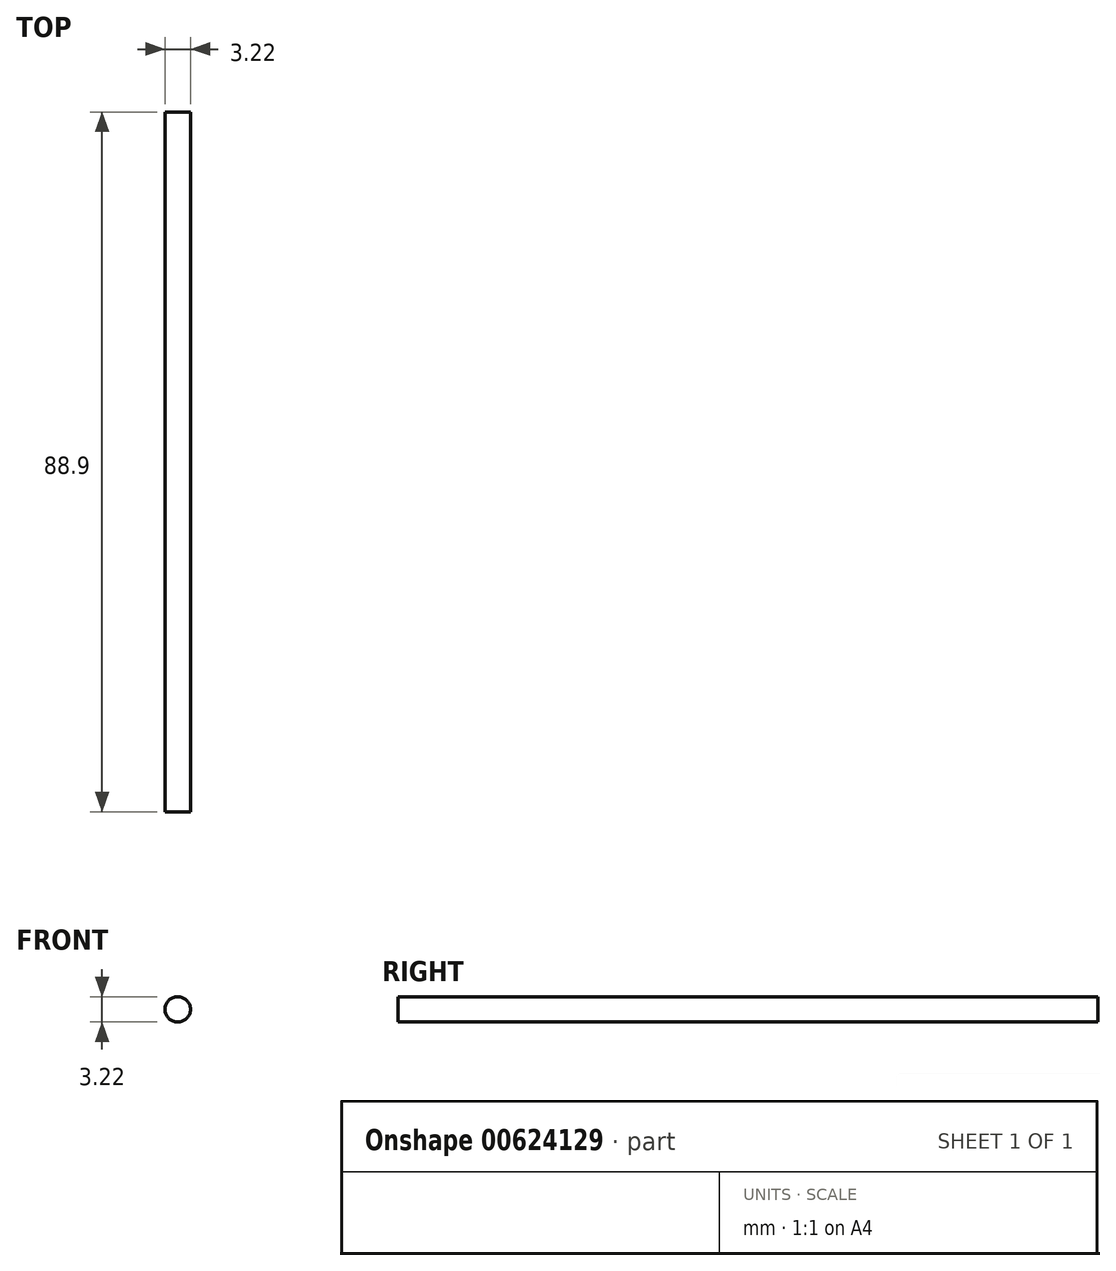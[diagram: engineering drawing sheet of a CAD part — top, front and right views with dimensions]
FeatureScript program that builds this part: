
annotation { "Feature Type Name" : "Feature", "Feature Type Description" : "" }
export const myFeature = defineFeature(function(context is Context, id is Id, definition is map)
    precondition{}
    {
        {
            var Q0;
            Q0=qCreatedBy(makeId("Front.planeOp"),FACE);
            var sketch = newSketch(context, id + "F0", { "sketchPlane" : qUnion([Q0])});
            skCircle(sketch, "E0", {"center": v(-63.51, 54.08) * mm, "radius": 1.61 * mm});
            skSolve(sketch);
        }
        {
            var Q0;
            Q0 = qSketchRegion(id + "F0", true);
            extrude(context, id + "F1", {"entities" : qUnion([Q0]), "depth" : 88.9 * mm, "offsetDistance" : 25.4 * mm});
        }
    });
